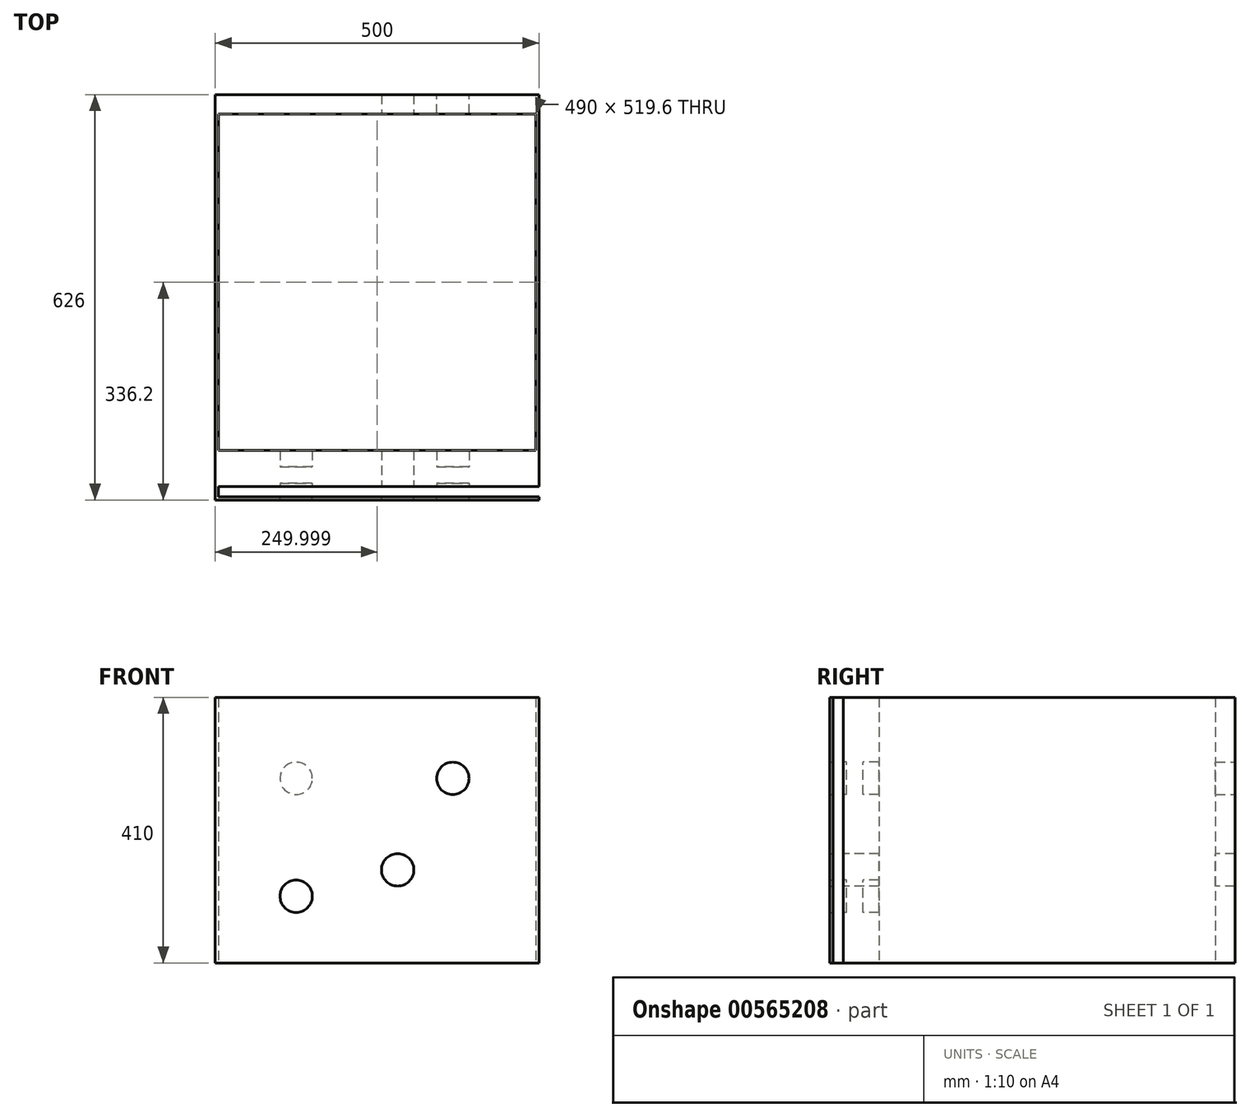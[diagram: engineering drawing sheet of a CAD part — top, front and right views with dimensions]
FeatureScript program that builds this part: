
annotation { "Feature Type Name" : "Feature", "Feature Type Description" : "" }
export const myFeature = defineFeature(function(context is Context, id is Id, definition is map)
    precondition{}
    {
        {
            var Q0;
            Q0=qCreatedBy(makeId("Front.planeOp"),FACE);
            var sketch = newSketch(context, id + "F0", { "sketchPlane" : qUnion([Q0])});
            skLineSegment(sketch, "E0.bottom", {"start": v(-123.13, -99.56) * mm, "end": v(376.87, -99.56) * mm});
            skLineSegment(sketch, "E0.top", {"start": v(-123.13, 310.44) * mm, "end": v(376.87, 310.44) * mm});
            skLineSegment(sketch, "E0.left", {"start": v(-123.13, -99.56) * mm, "end": v(-123.13, 310.44) * mm});
            skLineSegment(sketch, "E0.right", {"start": v(376.87, -99.56) * mm, "end": v(376.87, 310.44) * mm});
            skSolve(sketch);
        }
        {
            var Q0;
            Q0=qSketchRegion(id+"F0",true);
            extrude(context, id + "F1", {"entities" : qUnion([Q0]), "depth" : 5 * mm, "offsetDistance" : 25.4 * mm});
        }
        {
            var Q0;
            Q0=makeQuery(id+"F1.opExtrude","CAP_FACE",FACE,{"disambiguationData":[OSD([sQuery(id+"F0.wireOp",EDGE,"E0.bottom"),sQuery(id+"F0.wireOp",EDGE,"E0.top"),sQuery(id+"F0.wireOp",EDGE,"E0.left"),sQuery(id+"F0.wireOp",EDGE,"E0.right")])],"isStart":false});
            var sketch = newSketch(context, id + "F2", { "sketchPlane" : qUnion([Q0])});
            skPoint(sketch, "E1", {"position": v(1.87, 185.44) * mm});
            skPoint(sketch, "E2", {"position": v(1.87, 3.44) * mm});
            skPoint(sketch, "E3", {"position": v(243.87, 185.44) * mm});
            skPoint(sketch, "E4", {"position": v(158.67, 44.14) * mm});
            skCircle(sketch, "E5", {"center": v(1.87, 185.44) * mm, "radius": 25 * mm});
            skCircle(sketch, "E6", {"center": v(243.87, 185.44) * mm, "radius": 25 * mm});
            skCircle(sketch, "E7", {"center": v(1.87, 3.44) * mm, "radius": 25 * mm});
            skCircle(sketch, "E8", {"center": v(158.67, 44.14) * mm, "radius": 25 * mm});
            skLineSegment(sketch, "E9.bottom", {"start": v(-123.13, 310.44) * mm, "end": v(-118.13, 310.44) * mm});
            skLineSegment(sketch, "E9.top", {"start": v(-123.13, -99.56) * mm, "end": v(-118.13, -99.56) * mm});
            skLineSegment(sketch, "E9.left", {"start": v(-123.13, 310.44) * mm, "end": v(-123.13, -99.56) * mm});
            skLineSegment(sketch, "E9.right", {"start": v(-118.13, 310.44) * mm, "end": v(-118.13, -99.56) * mm});
            skSolve(sketch);
        }
        {
            var Q0;
            Q0=makeQuery(id+"F1.opExtrude","CAP_FACE",FACE,{"disambiguationData":[OSD([sQuery(id+"F0.wireOp",EDGE,"E0.bottom"),sQuery(id+"F0.wireOp",EDGE,"E0.top"),sQuery(id+"F0.wireOp",EDGE,"E0.left"),sQuery(id+"F0.wireOp",EDGE,"E0.right")])],"isStart":true});
            var sketch = newSketch(context, id + "F3", { "sketchPlane" : qUnion([Q0])});
            skLineSegment(sketch, "E10.bottom", {"start": v(-376.87, 310.44) * mm, "end": v(-371.87, 310.44) * mm});
            skLineSegment(sketch, "E10.top", {"start": v(-376.87, -99.56) * mm, "end": v(-371.87, -99.56) * mm});
            skLineSegment(sketch, "E10.left", {"start": v(-376.87, 310.44) * mm, "end": v(-376.87, -99.56) * mm});
            skLineSegment(sketch, "E10.right", {"start": v(-371.87, 310.44) * mm, "end": v(-371.87, -99.56) * mm});
            skLineSegment(sketch, "E11.bottom", {"start": v(123.13, 310.44) * mm, "end": v(118.13, 310.44) * mm});
            skLineSegment(sketch, "E11.top", {"start": v(123.13, -99.56) * mm, "end": v(118.13, -99.56) * mm});
            skLineSegment(sketch, "E11.left", {"start": v(123.13, 310.44) * mm, "end": v(123.13, -99.56) * mm});
            skLineSegment(sketch, "E11.right", {"start": v(118.13, 310.44) * mm, "end": v(118.13, -99.56) * mm});
            skSolve(sketch);
        }
        {
            var Q0;
            Q0=qSketchRegion(id+"F3",true);
            extrude(context, id + "F4", {"entities" : qUnion([Q0]), "operationType" : NewBodyOperationType.ADD, "depth" : 600 * mm, "offsetDistance" : 25.4 * mm});
        }
        {
            var Q0;
            Q0=makeQuery(id+"F4.opExtrude","SWEPT_FACE",FACE,{"disambiguationData":[OSD([sQuery(id+"F3.wireOp",EDGE,"E10.right")])]});
            var sketch = newSketch(context, id + "F5", { "sketchPlane" : qUnion([Q0])});
            skLineSegment(sketch, "E12.bottom", {"start": v(-600, 310.44) * mm, "end": v(-595, 310.44) * mm});
            skLineSegment(sketch, "E12.top", {"start": v(-600, -99.56) * mm, "end": v(-595, -99.56) * mm});
            skLineSegment(sketch, "E12.left", {"start": v(-600, 310.44) * mm, "end": v(-600, -99.56) * mm});
            skLineSegment(sketch, "E12.right", {"start": v(-595, 310.44) * mm, "end": v(-595, -99.56) * mm});
            skSolve(sketch);
        }
        {
            var Q0;
            Q0=qSketchRegion(id+"F5",true);
            extrude(context, id + "F6", {"entities" : qUnion([Q0]), "operationType" : NewBodyOperationType.ADD, "depth" : 491 * mm, "offsetDistance" : 25.4 * mm});
        }
        {
            var Q0;
            Q0=makeQuery(id+"F6.boolean.opBoolean","MERGE",FACE,{"derivedFrom":[makeQuery(id+"F4.opExtrude","CAP_FACE",FACE,{"disambiguationData":[OSD([sQuery(id+"F3.wireOp",EDGE,"E10.bottom"),sQuery(id+"F3.wireOp",EDGE,"E10.top"),sQuery(id+"F3.wireOp",EDGE,"E10.left"),sQuery(id+"F3.wireOp",EDGE,"E10.right")])],"isStart":false}),makeQuery(id+"F4.opExtrude","CAP_FACE",FACE,{"disambiguationData":[OSD([sQuery(id+"F3.wireOp",EDGE,"E11.bottom"),sQuery(id+"F3.wireOp",EDGE,"E11.top"),sQuery(id+"F3.wireOp",EDGE,"E11.left"),sQuery(id+"F3.wireOp",EDGE,"E11.right")])],"isStart":false}),makeQuery(id+"F6.opExtrude","SWEPT_FACE",FACE,{"disambiguationData":[OSD([sQuery(id+"F5.wireOp",EDGE,"E12.left")])]})]});
            var sketch = newSketch(context, id + "F7", { "sketchPlane" : qUnion([Q0])});
            skPoint(sketch, "E13", {"position": v(-1.87, 185.44) * mm});
            skCircle(sketch, "E14", {"center": v(-1.87, 185.44) * mm, "radius": 25 * mm});
            skPoint(sketch, "E15", {"position": v(-243.87, 185.44) * mm});
            skCircle(sketch, "E16", {"center": v(-243.87, 185.44) * mm, "radius": 25 * mm});
            skSolve(sketch);
        }
        {
            var Q0;
            Q0=makeQuery(id+"F2.imprint","IMPRINT",FACE,{"disambiguationData":[TD([[makeQuery(id+"F2.imprint","IMPRINT",EDGE,{"derivedFrom":sQuery(id+"F2.wireOp",EDGE,"E5")}),1.0]])]});
            extrude(context, id + "F8", {"entities" : qUnion([Q0]), "operationType" : NewBodyOperationType.REMOVE, "oppositeDirection" : true, "depth" : 25.4 * mm, "offsetDistance" : 25.4 * mm});
        }
        {
            var Q0;
            Q0=makeQuery(id+"F2.imprint","IMPRINT",FACE,{"disambiguationData":[TD([[makeQuery(id+"F2.imprint","IMPRINT",EDGE,{"derivedFrom":sQuery(id+"F2.wireOp",EDGE,"E6")}),1.0]])]});
            extrude(context, id + "F9", {"entities" : qUnion([Q0]), "operationType" : NewBodyOperationType.REMOVE, "oppositeDirection" : true, "depth" : 25.4 * mm, "offsetDistance" : 25.4 * mm});
        }
        {
            var Q0;
            Q0=makeQuery(id+"F2.imprint","IMPRINT",FACE,{"disambiguationData":[TD([[makeQuery(id+"F2.imprint","IMPRINT",EDGE,{"derivedFrom":sQuery(id+"F2.wireOp",EDGE,"E7")}),1.0]])]});
            extrude(context, id + "F10", {"entities" : qUnion([Q0]), "operationType" : NewBodyOperationType.REMOVE, "oppositeDirection" : true, "depth" : 25.4 * mm, "offsetDistance" : 25.4 * mm});
        }
        {
            var Q0;
            Q0=makeQuery(id+"F2.imprint","IMPRINT",FACE,{"disambiguationData":[TD([[makeQuery(id+"F2.imprint","IMPRINT",EDGE,{"derivedFrom":sQuery(id+"F2.wireOp",EDGE,"E9.bottom")}),-1.0]])]});
            extrude(context, id + "F11", {"entities" : qUnion([Q0]), "operationType" : NewBodyOperationType.ADD, "depth" : 21 * mm, "offsetDistance" : 25.4 * mm});
        }
        {
            var Q0;
            Q0=makeQuery(id+"F11.opExtrude","SWEPT_FACE",FACE,{"disambiguationData":[OSD([sQuery(id+"F2.wireOp",EDGE,"E9.right")])]});
            var sketch = newSketch(context, id + "F12", { "sketchPlane" : qUnion([Q0])});
            skLineSegment(sketch, "E17.bottom", {"start": v(-26, 310.44) * mm, "end": v(-21, 310.44) * mm});
            skLineSegment(sketch, "E17.top", {"start": v(-26, -99.56) * mm, "end": v(-21, -99.56) * mm});
            skLineSegment(sketch, "E17.left", {"start": v(-26, 310.44) * mm, "end": v(-26, -99.56) * mm});
            skLineSegment(sketch, "E17.right", {"start": v(-21, 310.44) * mm, "end": v(-21, -99.56) * mm});
            skSolve(sketch);
        }
        {
            var Q0;
            Q0=qSketchRegion(id+"F12",true);
            extrude(context, id + "F13", {"entities" : qUnion([Q0]), "operationType" : NewBodyOperationType.ADD, "depth" : 495 * mm, "offsetDistance" : 25.4 * mm});
        }
        {
            var Q0;
            Q0=makeQuery(id+"F2.imprint","IMPRINT",FACE,{"disambiguationData":[TD([[makeQuery(id+"F2.imprint","IMPRINT",EDGE,{"derivedFrom":sQuery(id+"F2.wireOp",EDGE,"E7")}),1.0]])]});
            extrude(context, id + "F14", {"entities" : qUnion([Q0]), "operationType" : NewBodyOperationType.REMOVE, "depth" : 76.2 * mm, "offsetDistance" : 25.4 * mm});
        }
        {
            var Q0;
            Q0=makeQuery(id+"F2.imprint","IMPRINT",FACE,{"disambiguationData":[TD([[makeQuery(id+"F2.imprint","IMPRINT",EDGE,{"derivedFrom":sQuery(id+"F2.wireOp",EDGE,"E8")}),1.0]])]});
            var Q1;
            Q1=sQuery(id+"F2.wireOp",EDGE,"E8");
            extrude(context, id + "F15", {"entities" : qUnion([Q0]), "operationType" : NewBodyOperationType.REMOVE, "surfaceEntities" : qUnion([Q1]), "depth" : 25.4 * mm, "offsetDistance" : 25.4 * mm});
        }
        {
            var Q0;
            Q0=makeQuery(id+"F6.opExtrude","SWEPT_FACE",FACE,{"disambiguationData":[OSD([sQuery(id+"F5.wireOp",EDGE,"E12.right")])]});
            extrude(context, id + "F16", {"entities" : qUnion([Q0]), "operationType" : NewBodyOperationType.ADD, "depth" : 25 * mm, "offsetDistance" : 25.4 * mm});
        }
        {
            var Q0;
            Q0=sQuery(id+"F7.wireOp",VERTEX,"E15");
            var Q1;
            Q1=makeQuery(id+"F1.opExtrude","SWEPT_BODY",BODY,{"disambiguationData":[OSD([sQuery(id+"F0.wireOp",EDGE,"E0.bottom"),sQuery(id+"F0.wireOp",EDGE,"E0.top"),sQuery(id+"F0.wireOp",EDGE,"E0.left"),sQuery(id+"F0.wireOp",EDGE,"E0.right")])]});
            hole(context, id + "F17", {"style" : HoleStyle.C_BORE, "endStyle" : HoleEndStyle.THROUGH, "holeDiameter" : 50 * mm, "cBoreDiameter" : 50 * mm, "cBoreDepth" : 0 * mm, "isTappedThrough" : true, "tappedDepth" : 12.7 * mm, "tapClearance" : 3, "startFromSketch" : true, "locations" : qUnion([Q0]), "scope" : qUnion([Q1])});
        }
        {
            var Q0;
            Q0=makeQuery(id+"F1.opExtrude","CAP_FACE",FACE,{"disambiguationData":[OSD([sQuery(id+"F0.wireOp",EDGE,"E0.bottom"),sQuery(id+"F0.wireOp",EDGE,"E0.top"),sQuery(id+"F0.wireOp",EDGE,"E0.left"),sQuery(id+"F0.wireOp",EDGE,"E0.right")])],"isStart":true});
            extrude(context, id + "F18", {"entities" : qUnion([Q0]), "operationType" : NewBodyOperationType.ADD, "depth" : 25 * mm, "offsetDistance" : 25.4 * mm});
        }
        {
            var Q0;
            Q0=makeQuery(id+"F18.opExtrude","CAP_FACE",FACE,{"disambiguationData":[OSD([sQuery(id+"F0.wireOp",EDGE,"E0.bottom"),sQuery(id+"F0.wireOp",EDGE,"E0.top"),sQuery(id+"F0.wireOp",EDGE,"E0.left"),sQuery(id+"F0.wireOp",EDGE,"E0.right")])],"isStart":false});
            var Q1;
            Q1 = qSketchRegion(id + "F0", true);
            extrude(context, id + "F19", {"entities" : qUnion([Q0, Q1]), "operationType" : NewBodyOperationType.ADD, "depth" : 25.4 * mm, "offsetDistance" : 25.4 * mm});
        }
        {
            var Q0;
            Q0=sQuery(id+"F2.wireOp",VERTEX,"E4");
            var Q1;
            Q1=makeQuery(id+"F1.opExtrude","SWEPT_BODY",BODY,{"disambiguationData":[OSD([sQuery(id+"F0.wireOp",EDGE,"E0.bottom"),sQuery(id+"F0.wireOp",EDGE,"E0.top"),sQuery(id+"F0.wireOp",EDGE,"E0.left"),sQuery(id+"F0.wireOp",EDGE,"E0.right")])]});
            hole(context, id + "F20", {"style" : HoleStyle.C_BORE, "endStyle" : HoleEndStyle.THROUGH, "holeDiameter" : 50 * mm, "cBoreDiameter" : 50 * mm, "cBoreDepth" : 0 * mm, "isTappedThrough" : true, "tappedDepth" : 12.7 * mm, "tapClearance" : 3, "startFromSketch" : true, "locations" : qUnion([Q0]), "scope" : qUnion([Q1])});
        }
    });
